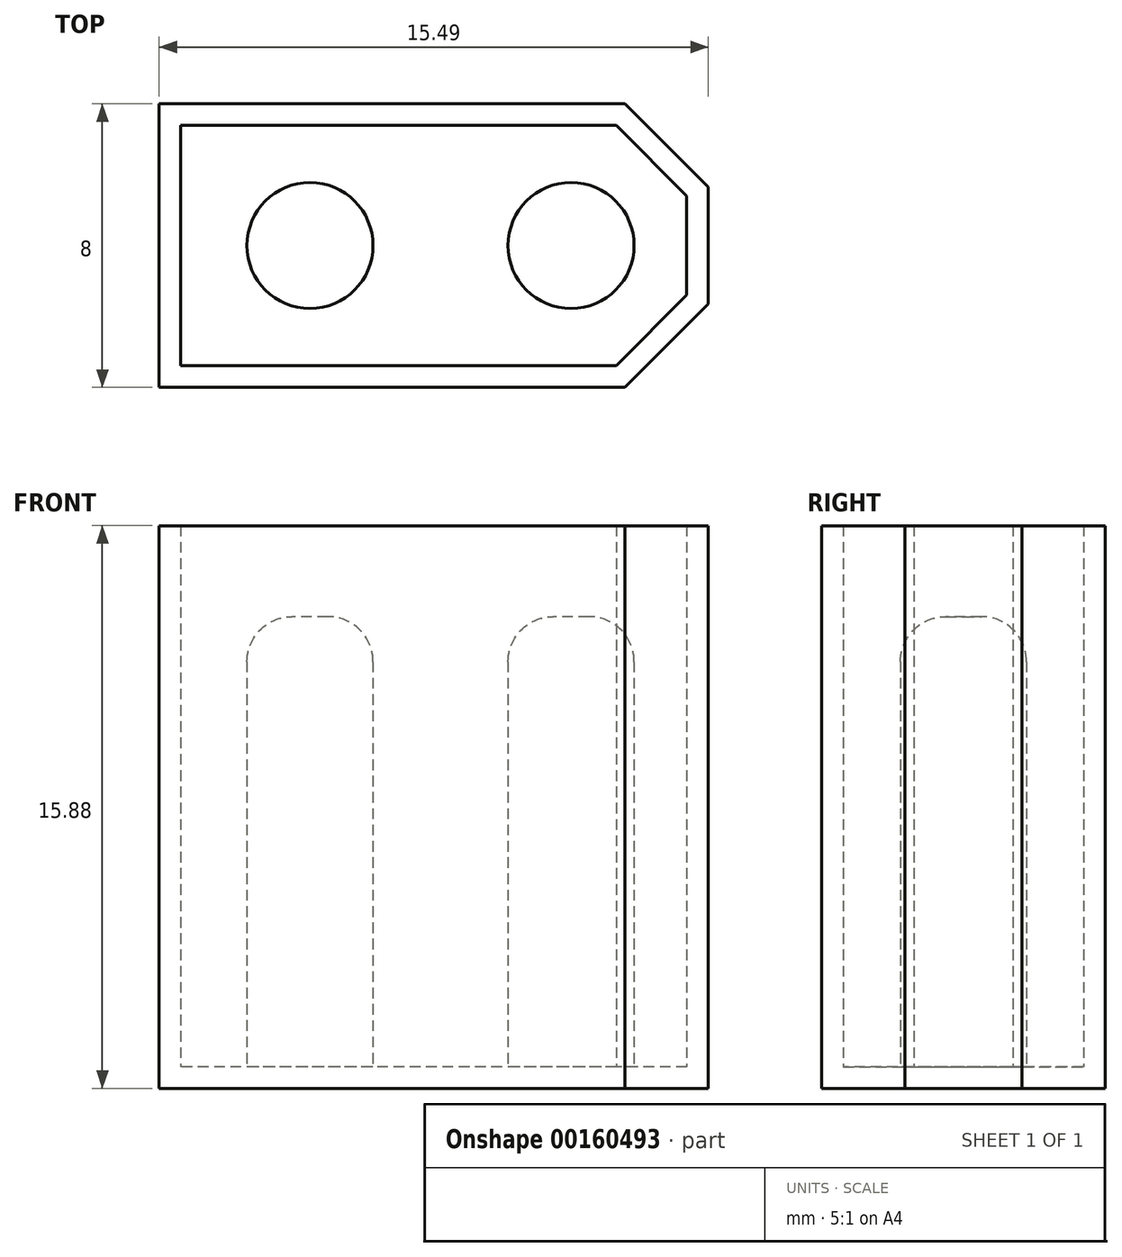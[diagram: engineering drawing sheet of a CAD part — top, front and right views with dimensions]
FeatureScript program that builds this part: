
annotation { "Feature Type Name" : "Feature", "Feature Type Description" : "" }
export const myFeature = defineFeature(function(context is Context, id is Id, definition is map)
    precondition{}
    {
        {
            var Q0;
            Q0=qCreatedBy(makeId("Top.planeOp"),FACE);
            var sketch = newSketch(context, id + "F0", { "sketchPlane" : qUnion([Q0])});
            skLineSegment(sketch, "E0", {"start": v(0, -4) * mm, "end": v(0, 4) * mm});
            skLineSegment(sketch, "E1", {"start": v(0, 4) * mm, "end": v(13.14, 4) * mm});
            skLineSegment(sketch, "E2", {"start": v(13.14, 4) * mm, "end": v(15.5, 1.65) * mm});
            skLineSegment(sketch, "E3", {"start": v(15.5, 1.65) * mm, "end": v(15.5, -1.65) * mm});
            skLineSegment(sketch, "E4", {"start": v(15.5, -1.65) * mm, "end": v(13.14, -4) * mm});
            skLineSegment(sketch, "E5", {"start": v(13.14, -4) * mm, "end": v(0, -4) * mm});
            skSolve(sketch);
        }
        {
            var Q0;
            Q0=qSketchRegion(id+"F0",true);
            extrude(context, id + "F1", {"entities" : qUnion([Q0]), "depth" : 15.88 * mm});
        }
        {
            var Q0;
            Q0=makeQuery(id+"F1.opExtrude","CAP_FACE",FACE,{"disambiguationData":[OSD([sQuery(id+"F0.wireOp",EDGE,"E0"),sQuery(id+"F0.wireOp",EDGE,"E1"),sQuery(id+"F0.wireOp",EDGE,"E2"),sQuery(id+"F0.wireOp",EDGE,"E3"),sQuery(id+"F0.wireOp",EDGE,"E4"),sQuery(id+"F0.wireOp",EDGE,"E5")])],"isStart":false});
            shell(context, id + "F2", {"entities" : qUnion([Q0]), "thickness" : 0.6 * mm});
        }
        {
            var Q0;
            Q0=makeQuery(id+"F2.opShell","OFFSET_FACE",FACE,{"disambiguationData":[OSD([sQuery(id+"F0.wireOp",EDGE,"E0"),sQuery(id+"F0.wireOp",EDGE,"E1"),sQuery(id+"F0.wireOp",EDGE,"E2"),sQuery(id+"F0.wireOp",EDGE,"E3"),sQuery(id+"F0.wireOp",EDGE,"E4"),sQuery(id+"F0.wireOp",EDGE,"E5")])]});
            var sketch = newSketch(context, id + "F3", { "sketchPlane" : qUnion([Q0])});
            skCircle(sketch, "E6", {"center": v(11.62, 0) * mm, "radius": 1.78 * mm});
            skCircle(sketch, "E7", {"center": v(4.25, 0) * mm, "radius": 1.78 * mm});
            skLineSegment(sketch, "E8", {"start": v(4.25, 0) * mm, "end": v(11.62, 0) * mm, "construction": true});
            skSolve(sketch);
        }
        {
            var Q0;
            Q0=qSketchRegion(id+"F3",true);
            extrude(context, id + "F4", {"entities" : qUnion([Q0]), "operationType" : NewBodyOperationType.ADD, "depth" : 12.7 * mm});
        }
        {
            var Q0;
            Q0=makeQuery(id+"F4.opExtrude","CAP_EDGE",EDGE,{"disambiguationData":[OSD([sQuery(id+"F3.wireOp",EDGE,"E7")])],"isStart":false});
            var Q1;
            Q1=makeQuery(id+"F4.opExtrude","CAP_EDGE",EDGE,{"disambiguationData":[OSD([sQuery(id+"F3.wireOp",EDGE,"E6")])],"isStart":false});
            fillet(context, id + "F5", {"entities" : qUnion([Q0, Q1]), "radius" : 1.27 * mm, "tangentPropagation" : true, "allowEdgeOverflow" : false});
        }
    });
